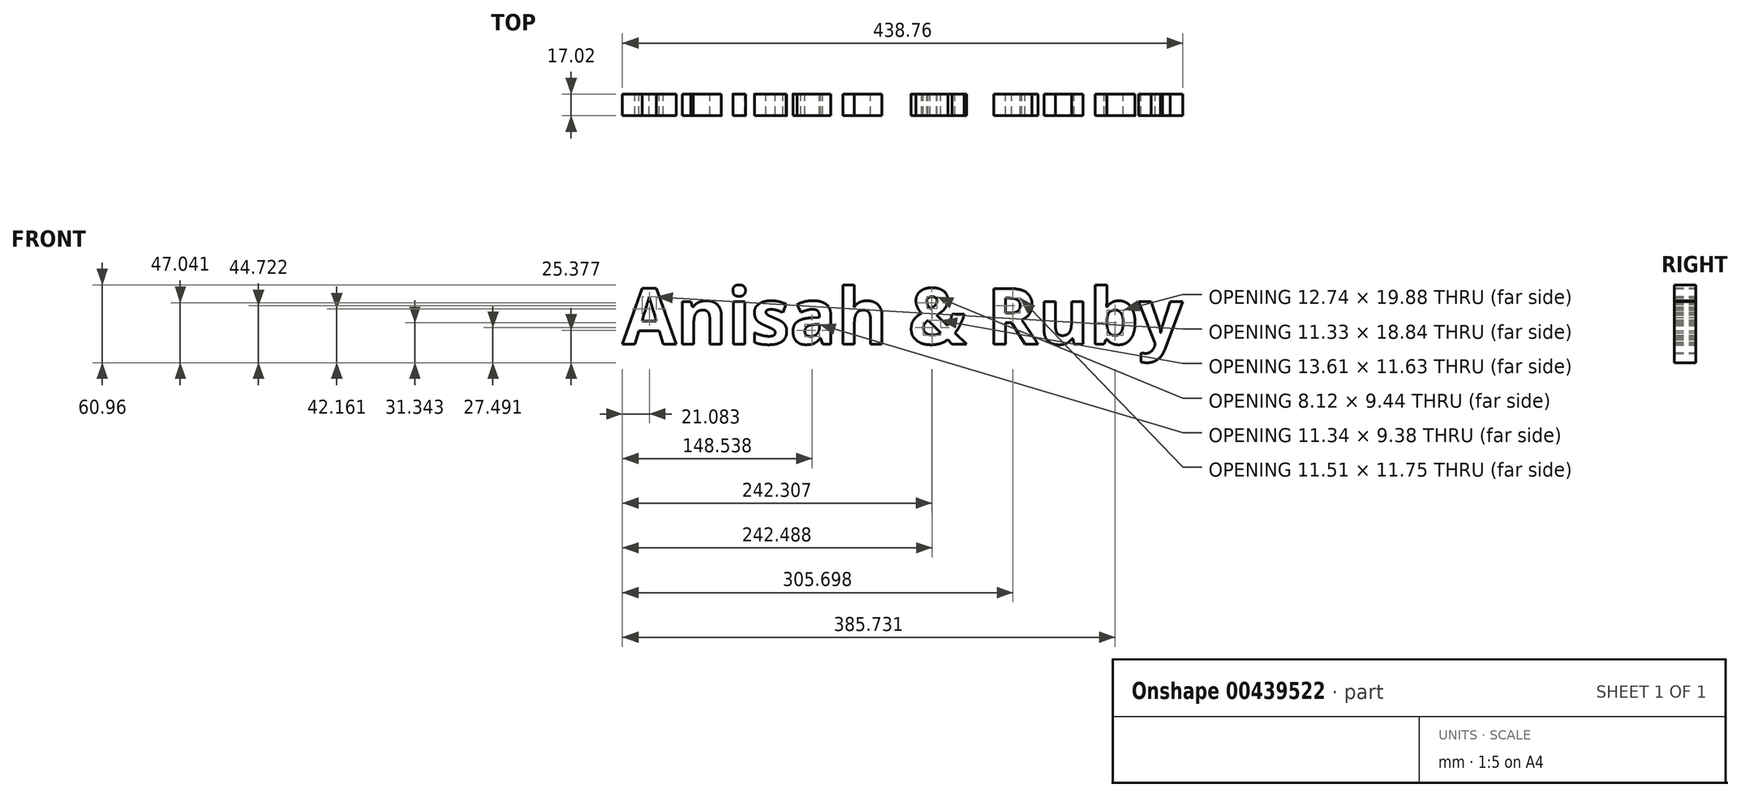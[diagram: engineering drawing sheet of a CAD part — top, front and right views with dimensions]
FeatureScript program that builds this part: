
annotation { "Feature Type Name" : "Feature", "Feature Type Description" : "" }
export const myFeature = defineFeature(function(context is Context, id is Id, definition is map)
    precondition{}
    {
        {
            var Q0;
            Q0=qCreatedBy(makeId("Front.planeOp"),FACE);
            var sketch = newSketch(context, id + "F0", { "sketchPlane" : qUnion([Q0])});
            skText(sketch, "E0", { "text": "Anisah & Ruby", "fontName": "OpenSans-Bold.ttf"});
            const initialGuessF0  = {"E0": [-0.0765, 0.01125, 1, 0, 0.04388]};
            skSetInitialGuess(sketch, initialGuessF0);
            skSolve(sketch);
        }
        {
            var Q0;
            Q0 = qSketchRegion(id + "F0", true);
            extrude(context, id + "F1", {"entities" : qUnion([Q0]), "depth" : 17.02 * mm});
        }
    });
